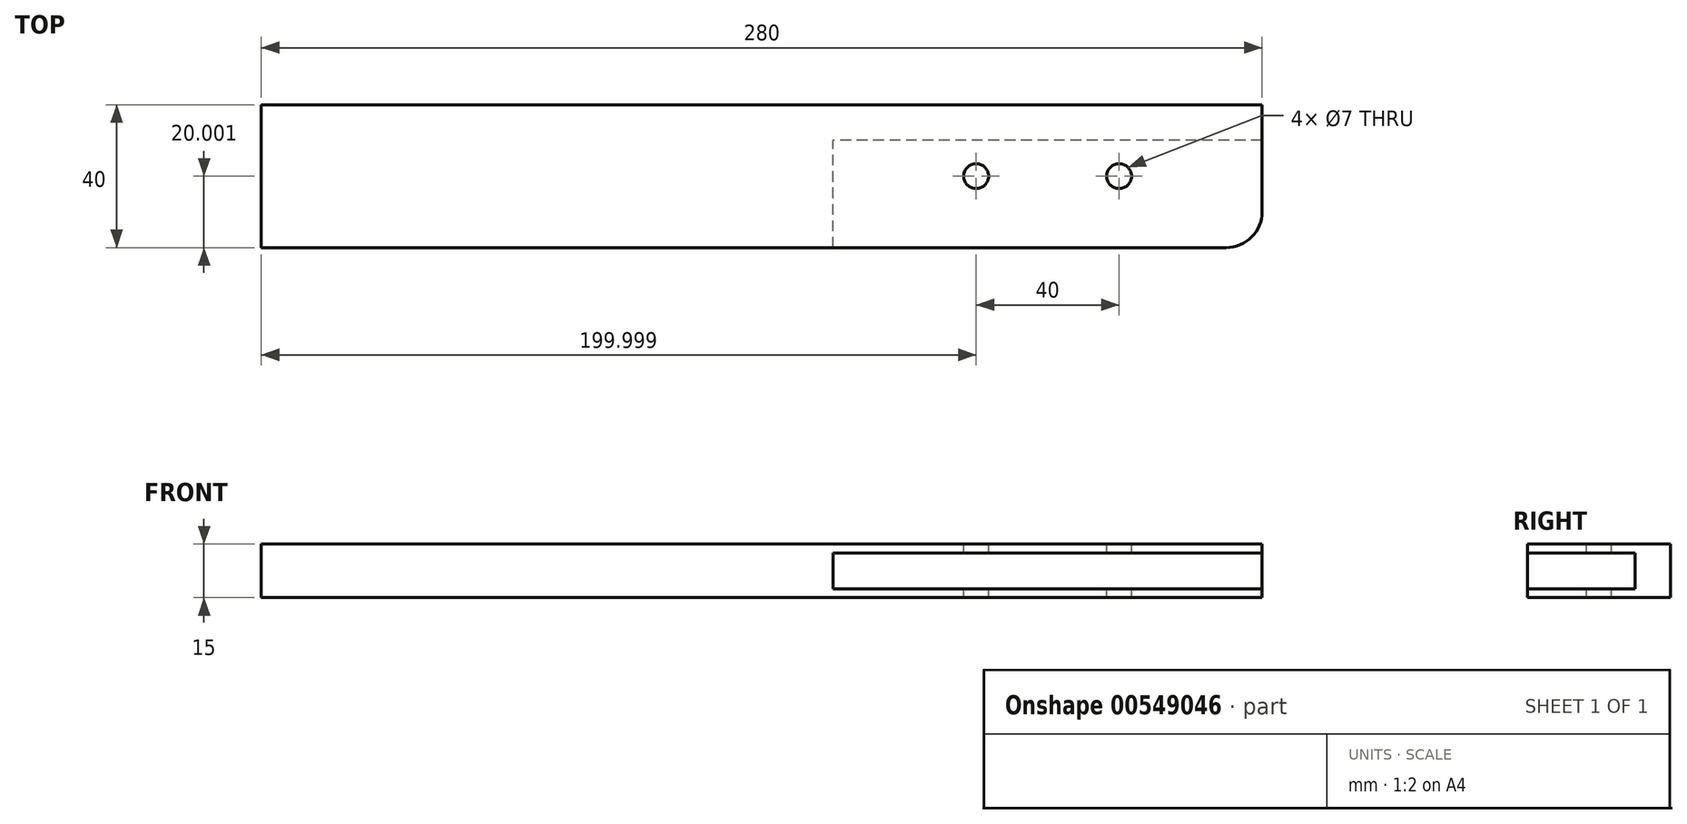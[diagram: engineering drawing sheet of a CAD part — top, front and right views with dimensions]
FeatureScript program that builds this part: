
annotation { "Feature Type Name" : "Feature", "Feature Type Description" : "" }
export const myFeature = defineFeature(function(context is Context, id is Id, definition is map)
    precondition{}
    {
        {
            var Q0;
            Q0=qCreatedBy(makeId("Top.planeOp"),FACE);
            var sketch = newSketch(context, id + "F0", { "sketchPlane" : qUnion([Q0])});
            skLineSegment(sketch, "E0", {"start": v(-120.93, 67.52) * mm, "end": v(159.07, 67.52) * mm});
            skLineSegment(sketch, "E1", {"start": v(-120.93, 67.52) * mm, "end": v(-120.93, 27.52) * mm});
            skLineSegment(sketch, "E2", {"start": v(-120.93, 27.52) * mm, "end": v(159.07, 27.52) * mm});
            skLineSegment(sketch, "E3", {"start": v(159.07, 27.52) * mm, "end": v(159.07, 67.52) * mm});
            skLineSegment(sketch, "E4", {"start": v(39.07, 27.52) * mm, "end": v(39.07, 57.52) * mm});
            skLineSegment(sketch, "E5", {"start": v(39.07, 57.52) * mm, "end": v(159.07, 57.52) * mm});
            skSolve(sketch);
        }
        {
            var Q0;
            {var subQ4=sQuery(id+"F0.wireOp",EDGE,"E0");Q0=makeQuery(id+"F0.imprint","IMPRINT",FACE,{"disambiguationData":[TD([[makeQuery(id+"F0.imprint","IMPRINT",EDGE,{"derivedFrom":subQ4}),-1.0]])]});}
            extrude(context, id + "F1", {"entities" : qUnion([Q0]), "depth" : 15 * mm, "offsetDistance" : 25 * mm});
        }
        {
            var Q0;
            {var subQ3=sQuery(id+"F0.wireOp",EDGE,"E4");Q0=makeQuery(id+"F0.imprint","IMPRINT",FACE,{"disambiguationData":[TD([[makeQuery(id+"F0.imprint","IMPRINT",EDGE,{"derivedFrom":subQ3}),-1.0]])]});}
            extrude(context, id + "F2", {"entities" : qUnion([Q0]), "operationType" : NewBodyOperationType.ADD, "depth" : 2.5 * mm, "offsetDistance" : 25 * mm});
        }
        {
            var Q0;
            Q0=makeQuery(id+"F1.opExtrude","SWEPT_FACE",FACE,{"disambiguationData":[OSD([sQuery(id+"F0.wireOp",EDGE,"E5")])]});
            var sketch = newSketch(context, id + "F3", { "sketchPlane" : qUnion([Q0])});
            skLineSegment(sketch, "E6", {"start": v(159.07, 15) * mm, "end": v(159.07, 12.5) * mm});
            skLineSegment(sketch, "E7", {"start": v(159.07, 12.5) * mm, "end": v(39.07, 12.5) * mm});
            skLineSegment(sketch, "E8", {"start": v(39.07, 12.5) * mm, "end": v(39.07, 15) * mm});
            skLineSegment(sketch, "E9", {"start": v(39.07, 15) * mm, "end": v(159.07, 15) * mm});
            skLineSegment(sketch, "E10", {"start": v(39.07, 15) * mm, "end": v(159.07, 15) * mm, "construction": true});
            skSolve(sketch);
        }
        {
            var Q0;
            Q0=makeQuery(id+"F3.imprint","IMPRINT",FACE,{"disambiguationData":[TD([[makeQuery(id+"F3.imprint","IMPRINT",EDGE,{"derivedFrom":sQuery(id+"F3.wireOp",EDGE,"E6")}),-1.0]])]});
            extrude(context, id + "F4", {"entities" : qUnion([Q0]), "operationType" : NewBodyOperationType.ADD, "depth" : 30 * mm, "offsetDistance" : 25 * mm});
        }
        {
            var Q0;
            Q0=makeQuery(id+"F4.opExtrude","CAP_EDGE",EDGE,{"disambiguationData":[OSD([sQuery(id+"F3.wireOp",EDGE,"E6")])],"isStart":false});
            var Q1;
            Q1=makeQuery(id+"F2.opExtrude","SWEPT_EDGE",EDGE,{"disambiguationData":[OSD([sQuery(id+"F0.wireOp",EDGE,"E2"),sQuery(id+"F0.wireOp",EDGE,"E3")])]});
            fillet(context, id + "F5", {"entities" : qUnion([Q0, Q1]), "radius" : 10 * mm, "tangentPropagation" : true, "allowEdgeOverflow" : false});
        }
        {
            var Q0;
            Q0=makeQuery(id+"F4.boolean.opBoolean","MERGE",FACE,{"derivedFrom":[makeQuery(id+"F1.opExtrude","CAP_FACE",FACE,{"disambiguationData":[OSD([sQuery(id+"F0.wireOp",EDGE,"E0"),sQuery(id+"F0.wireOp",EDGE,"E1"),sQuery(id+"F0.wireOp",EDGE,"E2"),sQuery(id+"F0.wireOp",EDGE,"E3"),sQuery(id+"F0.wireOp",EDGE,"E4"),sQuery(id+"F0.wireOp",EDGE,"E5")])],"isStart":false}),makeQuery(id+"F4.opExtrude","SWEPT_FACE",FACE,{"disambiguationData":[OSD([sQuery(id+"F3.wireOp",EDGE,"E9")])]})]});
            var sketch = newSketch(context, id + "F6", { "sketchPlane" : qUnion([Q0])});
            skCircle(sketch, "E11", {"center": v(79.07, 47.52) * mm, "radius": 3.5 * mm});
            skCircle(sketch, "E12", {"center": v(119.07, 47.52) * mm, "radius": 3.5 * mm});
            skSolve(sketch);
        }
        {
            var Q0;
            Q0 = qSketchRegion(id + "F6", true);
            extrude(context, id + "F7", {"entities" : qUnion([Q0]), "operationType" : NewBodyOperationType.REMOVE, "oppositeDirection" : true, "depth" : 25 * mm, "offsetDistance" : 25 * mm});
        }
    });
